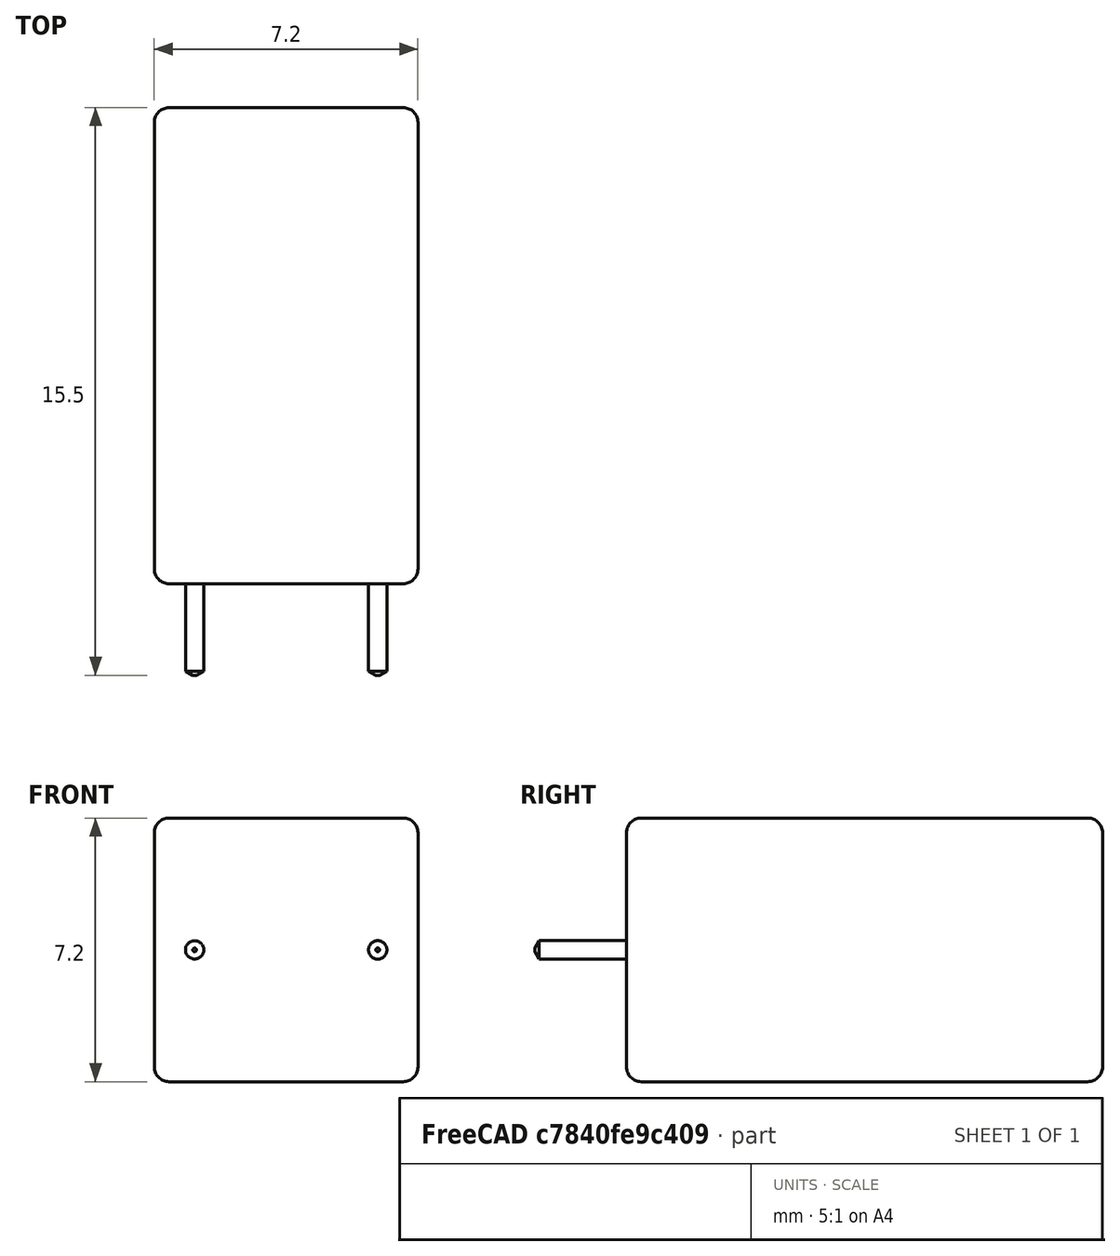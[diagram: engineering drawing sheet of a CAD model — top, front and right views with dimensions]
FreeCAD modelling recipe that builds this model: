
FCSTD DOCUMENT  (FreeCAD 0.17R13528 (Git))
Label: WIMA_K_Case
License: All rights reserved
LicenseURL: http://en.wikipedia.org/wiki/All_rights_reserved
objects: Part::Part2DObjectPython×6, Part::Feature×1
note: 7 computed .brp shape members not serialized (recipe doc carries the construction recipe); baked Part::Feature solids carry a one-line shape summary decoded from their .brp

FEATURE [Part::Part2DObjectPython] ShapeString  label="F_WIMA"  # Draft 2D object (typed FeaturePython)
  FontFile = <userpath>/Desktop/Freecad Projects/calibrib.ttf
  Placement = pos=(-0.75,3.5,3.61) rot=(0,0,1;0rad)
  Size = 1.75
  String = WIMA
  Tracking = 0
FEATURE [Part::Part2DObjectPython] ShapeString001  label="F_Vaule/Rating"  # Draft 2D object (typed FeaturePython)
  FontFile = <userpath>/Desktop/Freecad Projects/calibrib.ttf
  Placement = pos=(-0.65,2.25,3.61) rot=(0,0,1;0rad)
  Size = 1
  String = 2.2µ/63V
  Tracking = 0
FEATURE [Part::Part2DObjectPython] ShapeString002  label="F_Tolerance"  # Draft 2D object (typed FeaturePython)
  FontFile = <userpath>/Desktop/Freecad Projects/calibrib.ttf
  Placement = pos=(-0.65,1,3.61) rot=(0,0,1;0rad)
  Size = 1
  String = 10
  Tracking = 0
FEATURE [Part::Part2DObjectPython] ShapeString003  label="B_WIMA"  # Draft 2D object (typed FeaturePython)
  FontFile = <userpath>/Desktop/Freecad Projects/calibrib.ttf
  Placement = pos=(5,3.5,-3.61) rot=(0,1,0;3.14159rad)
  Size = 1.75
  String = WIMA
  Tracking = 0
FEATURE [Part::Part2DObjectPython] ShapeString004  label="B_Value/Tolerance"  # Draft 2D object (typed FeaturePython)
  FontFile = <userpath>/Desktop/Freecad Projects/calibrib.ttf
  Placement = pos=(4.9,2.25,-3.61) rot=(0,1,0;3.14159rad)
  Size = 1
  String = 2.2µ/63V
  Tracking = 0
FEATURE [Part::Part2DObjectPython] ShapeString005  label="B_Tolerance"  # Draft 2D object (typed FeaturePython)
  FontFile = <userpath>/Desktop/Freecad Projects/calibrib.ttf
  Placement = pos=(4.9,1,-3.61) rot=(0,1,0;3.14159rad)
  Size = 1
  String = 10
  Tracking = 0
FEATURE [Part::Feature] Part__Feature001  label="WIMA_K_Case"
  shape: bbox 7.2 x 15.5 x 7.2 mm, 36 faces (baked)
